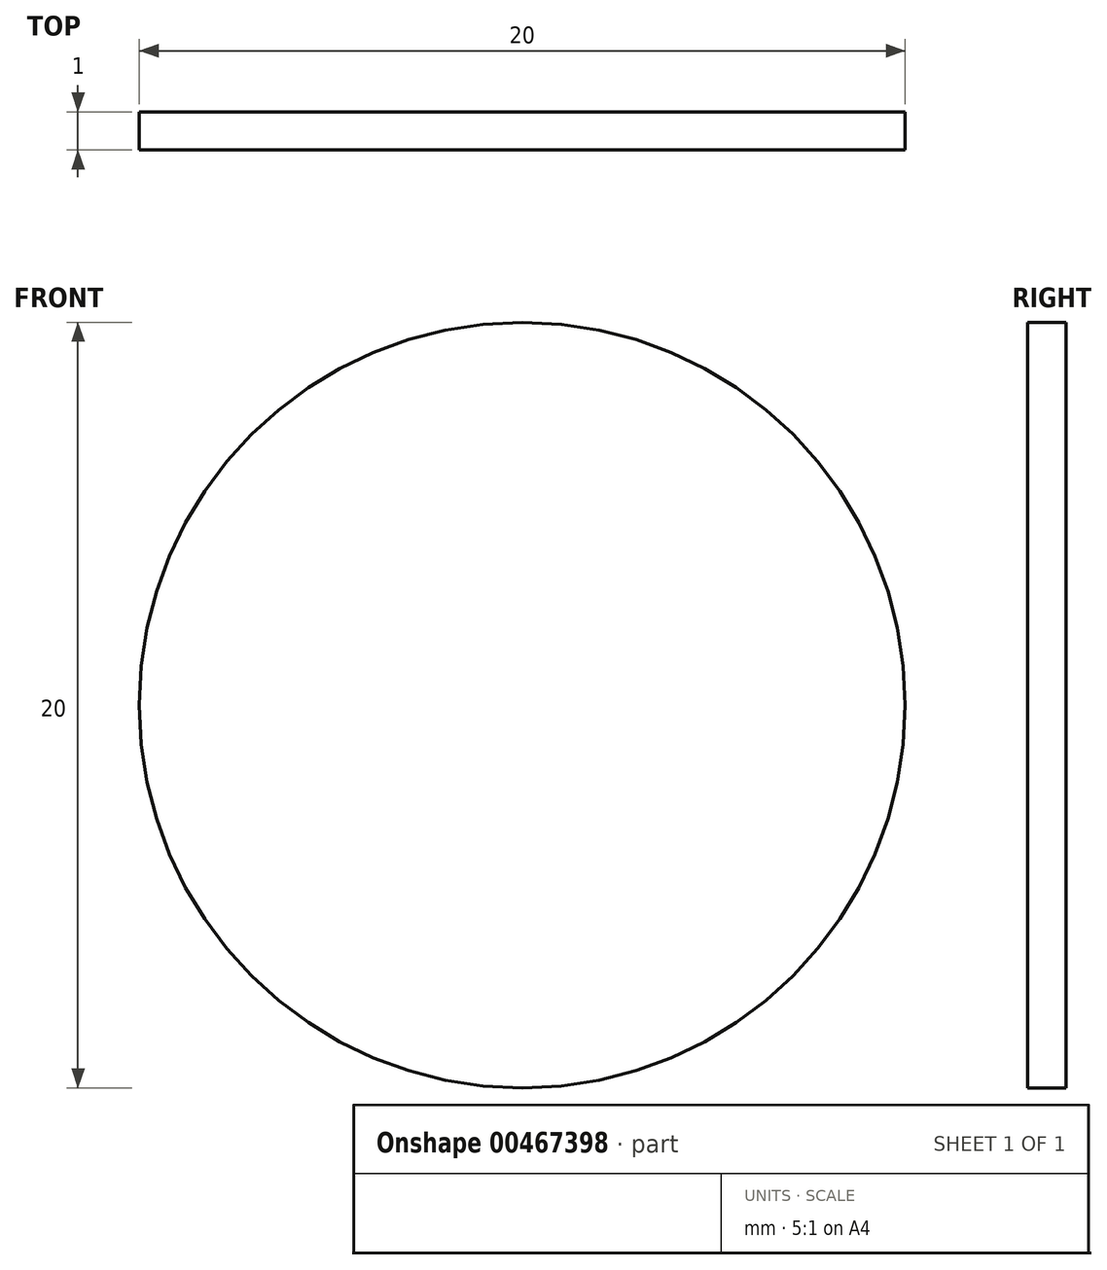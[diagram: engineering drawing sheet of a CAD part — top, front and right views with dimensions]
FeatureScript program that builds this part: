
annotation { "Feature Type Name" : "Feature", "Feature Type Description" : "" }
export const myFeature = defineFeature(function(context is Context, id is Id, definition is map)
    precondition{}
    {
        {
            var Q0;
            Q0=qCreatedBy(makeId("Front.planeOp"),FACE);
            var sketch = newSketch(context, id + "F0", { "sketchPlane" : qUnion([Q0])});
            skCircle(sketch, "E0", {"center": v(0, 0) * mm, "radius": 10 * mm});
            skSolve(sketch);
        }
        {
            var Q0;
            Q0=makeQuery(id+"F0.imprint","IMPRINT",FACE,{"disambiguationData":[TD([[makeQuery(id+"F0.imprint","IMPRINT",EDGE,{"derivedFrom":sQuery(id+"F0.wireOp",EDGE,"E0")}),1.0]])]});
            extrude(context, id + "F1", {"entities" : qUnion([Q0]), "depth" : 1 * mm, "offsetDistance" : 25 * mm});
        }
    });
